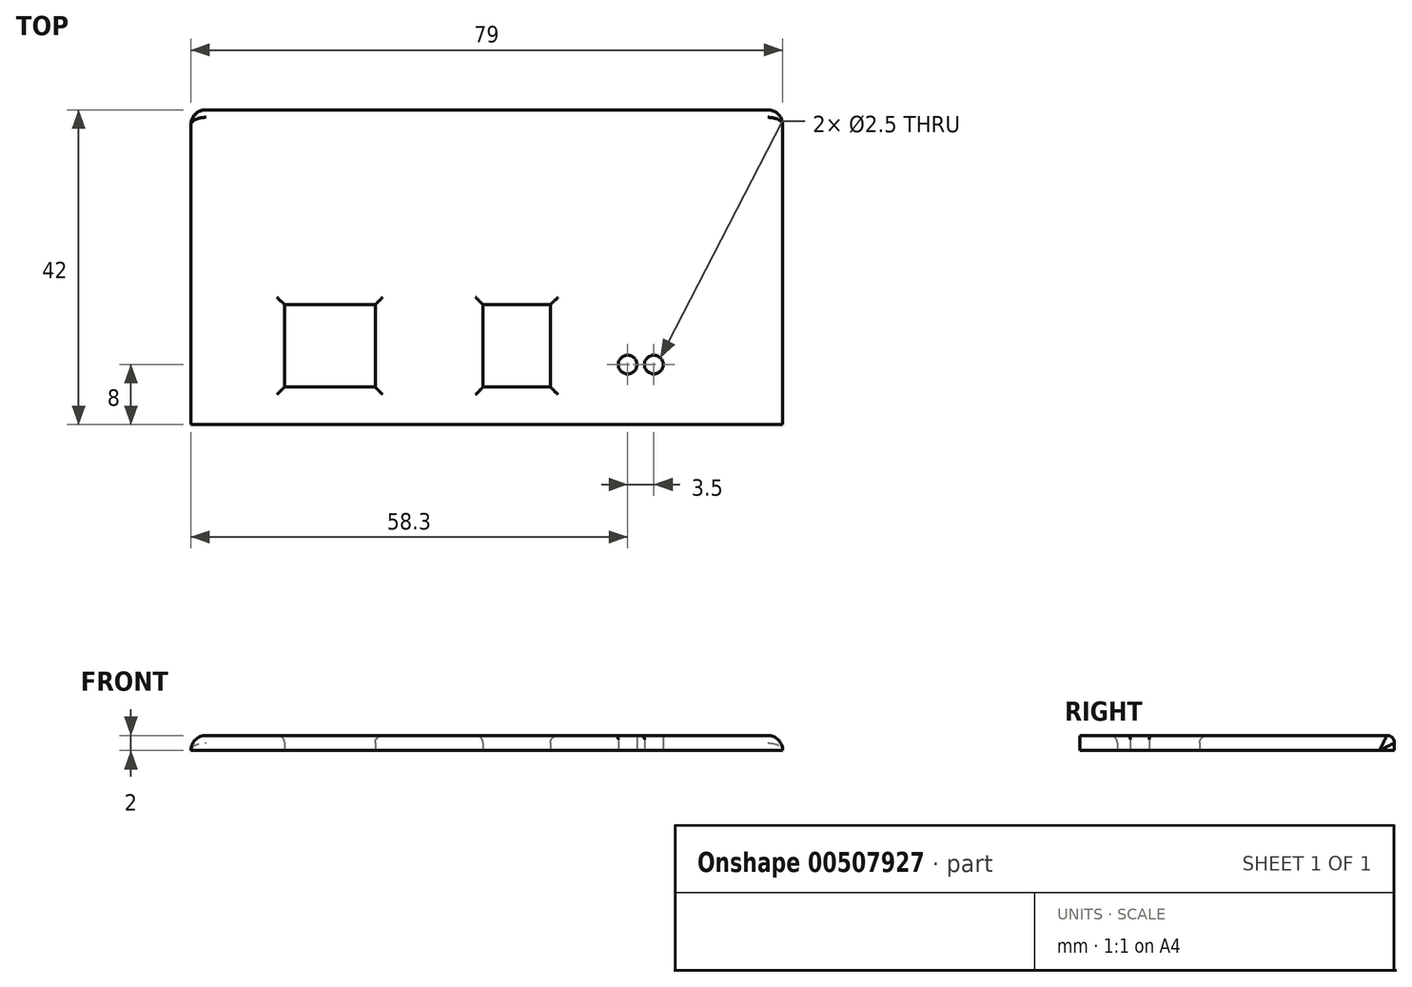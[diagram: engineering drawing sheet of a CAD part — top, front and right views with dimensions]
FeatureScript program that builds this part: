
annotation { "Feature Type Name" : "Feature", "Feature Type Description" : "" }
export const myFeature = defineFeature(function(context is Context, id is Id, definition is map)
    precondition{}
    {
        {
            var Q0;
            Q0=qCreatedBy(makeId("Top.planeOp"),FACE);
            var sketch = newSketch(context, id + "F0", { "sketchPlane" : qUnion([Q0])});
            skLineSegment(sketch, "E0.bottom", {"start": v(-39.5, 21) * mm, "end": v(39.5, 21) * mm});
            skLineSegment(sketch, "E0.top", {"start": v(-39.5, -21) * mm, "end": v(39.5, -21) * mm});
            skLineSegment(sketch, "E0.left", {"start": v(-39.5, 21) * mm, "end": v(-39.5, -21) * mm});
            skLineSegment(sketch, "E0.right", {"start": v(39.5, 21) * mm, "end": v(39.5, -21) * mm});
            skPoint(sketch, "E0.middle", {"position": v(0, 0) * mm});
            skLineSegment(sketch, "E1.0", {"start": v(-39.5, -5) * mm, "end": v(39.5, -5) * mm, "construction": true});
            skLineSegment(sketch, "E2.0", {"start": v(-39.5, -16) * mm, "end": v(39.5, -16) * mm, "construction": true});
            skLineSegment(sketch, "E3", {"start": v(-39.5, -11) * mm, "end": v(-27, -11) * mm, "construction": true});
            skLineSegment(sketch, "E4", {"start": v(-27, -11) * mm, "end": v(-14.9, -11) * mm, "construction": true});
            skLineSegment(sketch, "E5", {"start": v(-27, -11) * mm, "end": v(-0.5, -11) * mm, "construction": true});
            skLineSegment(sketch, "E6", {"start": v(-0.5, -11) * mm, "end": v(8.5, -11) * mm, "construction": true});
            skLineSegment(sketch, "E7", {"start": v(-27, -11) * mm, "end": v(18.8, -11) * mm, "construction": true});
            skLineSegment(sketch, "E8", {"start": v(18.8, -11) * mm, "end": v(22.3, -11) * mm, "construction": true});
            skLineSegment(sketch, "E9", {"start": v(22.3, -11) * mm, "end": v(22.3, -13) * mm, "construction": true});
            skLineSegment(sketch, "E10", {"start": v(18.8, -11) * mm, "end": v(18.8, -13) * mm, "construction": true});
            skCircle(sketch, "E11", {"center": v(22.3, -13) * mm, "radius": 1.25 * mm});
            skCircle(sketch, "E12", {"center": v(18.8, -13) * mm, "radius": 1.25 * mm});
            skLineSegment(sketch, "E13", {"start": v(-27, -11) * mm, "end": v(-27, -5) * mm});
            skLineSegment(sketch, "E14", {"start": v(-27, -11) * mm, "end": v(-27, -16) * mm});
            skLineSegment(sketch, "E15", {"start": v(-14.9, -11) * mm, "end": v(-14.9, -5) * mm});
            skLineSegment(sketch, "E16", {"start": v(-14.9, -11) * mm, "end": v(-14.9, -16) * mm});
            skLineSegment(sketch, "E17", {"start": v(-27, -5) * mm, "end": v(-14.9, -5) * mm});
            skLineSegment(sketch, "E18", {"start": v(-27, -16) * mm, "end": v(-14.9, -16) * mm});
            skLineSegment(sketch, "E19", {"start": v(-0.5, -11) * mm, "end": v(-0.5, -16) * mm});
            skLineSegment(sketch, "E20", {"start": v(8.5, -11) * mm, "end": v(8.5, -16) * mm});
            skLineSegment(sketch, "E21", {"start": v(-0.5, -16) * mm, "end": v(8.5, -16) * mm});
            skLineSegment(sketch, "E22", {"start": v(-0.5, -11) * mm, "end": v(-0.5, -5) * mm});
            skLineSegment(sketch, "E23", {"start": v(8.5, -11) * mm, "end": v(8.5, -5) * mm});
            skLineSegment(sketch, "E24", {"start": v(-0.5, -5) * mm, "end": v(8.5, -5) * mm});
            skSolve(sketch);
        }
        {
            var Q0;
            Q0=makeQuery(id+"F0.imprint","IMPRINT",FACE,{"disambiguationData":[TD([[makeQuery(id+"F0.imprint","IMPRINT",EDGE,{"derivedFrom":sQuery(id+"F0.wireOp",EDGE,"E0.bottom")}),-1.0]])]});
            extrude(context, id + "F1", {"entities" : qUnion([Q0]), "depth" : 2 * mm});
        }
        {
            var Q0;
            Q0=makeQuery(id+"F1.opExtrude","CAP_EDGE",EDGE,{"disambiguationData":[OSD([sQuery(id+"F0.wireOp",EDGE,"E17")])],"isStart":false});
            var Q1;
            Q1=makeQuery(id+"F1.opExtrude","CAP_EDGE",EDGE,{"disambiguationData":[OSD([sQuery(id+"F0.wireOp",EDGE,"E18")])],"isStart":false});
            var Q2;
            Q2=makeQuery(id+"F1.opExtrude","CAP_EDGE",EDGE,{"disambiguationData":[OSD([sQuery(id+"F0.wireOp",EDGE,"E13"),sQuery(id+"F0.wireOp",EDGE,"E14")])],"isStart":false});
            var Q3;
            Q3=makeQuery(id+"F1.opExtrude","CAP_EDGE",EDGE,{"disambiguationData":[OSD([sQuery(id+"F0.wireOp",EDGE,"E15"),sQuery(id+"F0.wireOp",EDGE,"E16")])],"isStart":false});
            var Q4;
            Q4=makeQuery(id+"F1.opExtrude","CAP_EDGE",EDGE,{"disambiguationData":[OSD([sQuery(id+"F0.wireOp",EDGE,"IXNn87ag-Z6Fj-s0Qp-cjCS-UG6cs4xpn5Du"),sQuery(id+"F0.wireOp",EDGE,"E19")])],"isStart":false});
            var Q5;
            Q5=makeQuery(id+"F1.opExtrude","CAP_EDGE",EDGE,{"disambiguationData":[OSD([sQuery(id+"F0.wireOp",EDGE,"E21")])],"isStart":false});
            var Q6;
            Q6=makeQuery(id+"F1.opExtrude","CAP_EDGE",EDGE,{"disambiguationData":[OSD([sQuery(id+"F0.wireOp",EDGE,"P5WaOOkt-1sTi-gfa5-lV5l-aZJqf2SfJz9l")])],"isStart":false});
            var Q7;
            Q7=makeQuery(id+"F1.opExtrude","CAP_EDGE",EDGE,{"disambiguationData":[OSD([sQuery(id+"F0.wireOp",EDGE,"oXHxsYbY-Ua07-kXpE-Iemr-8acgqE4yo465"),sQuery(id+"F0.wireOp",EDGE,"E20")])],"isStart":false});
            var Q8;
            Q8=makeQuery(id+"F1.opExtrude","CAP_EDGE",EDGE,{"disambiguationData":[OSD([sQuery(id+"F0.wireOp",EDGE,"E0.bottom")])],"isStart":false});
            var Q9;
            Q9=makeQuery(id+"F1.opExtrude","CAP_EDGE",EDGE,{"disambiguationData":[OSD([sQuery(id+"F0.wireOp",EDGE,"E24")])],"isStart":false});
            fillet(context, id + "F2", {"entities" : qUnion([Q0, Q1, Q2, Q3, Q4, Q5, Q6, Q7, Q8, Q9]), "radius" : 1 * mm, "tangentPropagation" : true, "allowEdgeOverflow" : false});
        }
        {
            var Q0;
            Q0=makeQuery(id+"F1.opExtrude","CAP_EDGE",EDGE,{"disambiguationData":[OSD([sQuery(id+"F0.wireOp",EDGE,"E0.left")])],"isStart":false});
            var Q1;
            Q1=makeQuery(id+"F1.opExtrude","CAP_EDGE",EDGE,{"disambiguationData":[OSD([sQuery(id+"F0.wireOp",EDGE,"E0.right")])],"isStart":false});
            fillet(context, id + "F3", {"entities" : qUnion([Q0, Q1]), "radius" : 2 * mm, "tangentPropagation" : true, "allowEdgeOverflow" : false});
        }
        {
            var Q0;
            Q0=makeQuery(id+"F1.opExtrude","CAP_EDGE",EDGE,{"disambiguationData":[OSD([sQuery(id+"F0.wireOp",EDGE,"E12")])],"isStart":false});
            var Q1;
            Q1=makeQuery(id+"F1.opExtrude","CAP_EDGE",EDGE,{"disambiguationData":[OSD([sQuery(id+"F0.wireOp",EDGE,"E11")])],"isStart":false});
            fillet(context, id + "F4", {"entities" : qUnion([Q0, Q1]), "radius" : .5 * mm, "tangentPropagation" : true, "allowEdgeOverflow" : false});
        }
    });
